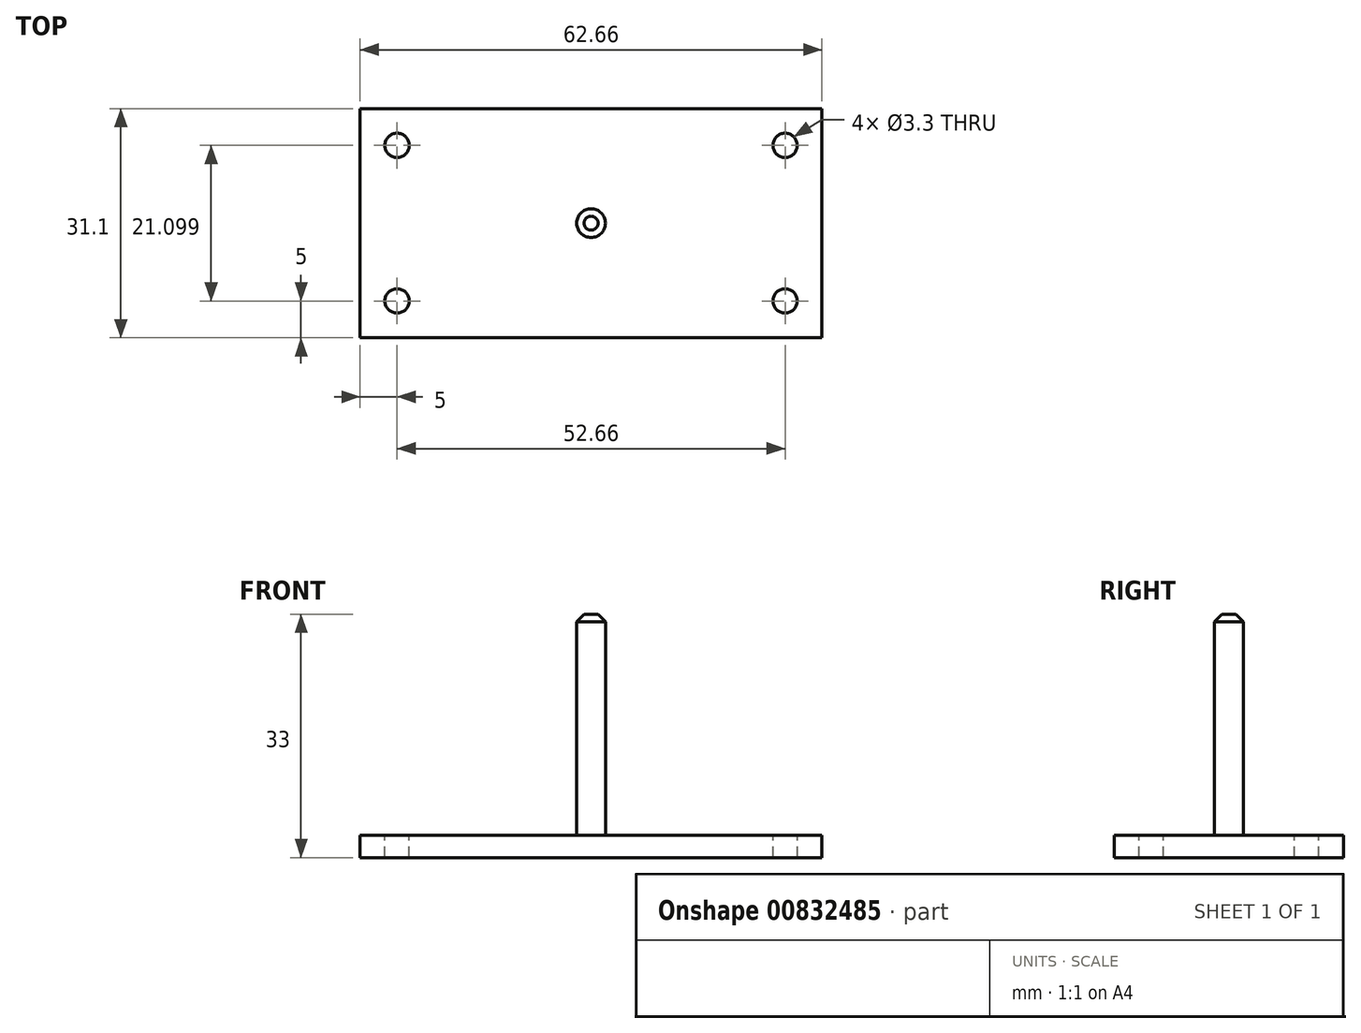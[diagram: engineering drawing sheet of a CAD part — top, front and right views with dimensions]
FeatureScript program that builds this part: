
annotation { "Feature Type Name" : "Feature", "Feature Type Description" : "" }
export const myFeature = defineFeature(function(context is Context, id is Id, definition is map)
    precondition{}
    {
        {
            var Q0;
            Q0=qCreatedBy(makeId("Top.planeOp"),FACE);
            var sketch = newSketch(context, id + "F0", { "sketchPlane" : qUnion([Q0])});
            skCircle(sketch, "E0", {"center": v(0, 0) * mm, "radius": 15 * mm});
            skCircle(sketch, "E1", {"center": v(0, 0) * mm, "radius": 1.95 * mm});
            skLineSegment(sketch, "E2.bottom", {"start": v(31.33, -15.55) * mm, "end": v(-31.33, -15.55) * mm});
            skLineSegment(sketch, "E2.top", {"start": v(31.33, 15.55) * mm, "end": v(-31.33, 15.55) * mm});
            skLineSegment(sketch, "E2.left", {"start": v(31.33, -15.55) * mm, "end": v(31.33, 15.55) * mm});
            skLineSegment(sketch, "E2.right", {"start": v(-31.33, -15.55) * mm, "end": v(-31.33, 15.55) * mm});
            skPoint(sketch, "E3", {"position": v(26.33, 10.55) * mm});
            skLineSegment(sketch, "E4", {"start": v(0, 13.06) * mm, "end": v(0, -9.28) * mm, "construction": true});
            skLineSegment(sketch, "E5", {"start": v(-7.34, 0) * mm, "end": v(7.3, 0) * mm, "construction": true});
            skPoint(sketch, "E6.MirrorP", {"position": v(-26.33, 10.55) * mm});
            skPoint(sketch, "E7.MirrorP", {"position": v(26.33, -10.55) * mm});
            skPoint(sketch, "E8.MirrorP", {"position": v(-26.33, -10.55) * mm});
            skSolve(sketch);
        }
        {
            var Q0;
            Q0=makeQuery(id+"F0.imprint","IMPRINT",FACE,{"disambiguationData":[TD([[makeQuery(id+"F0.imprint","IMPRINT",EDGE,{"derivedFrom":sQuery(id+"F0.wireOp",EDGE,"E1")}),1.0]])]});
            var Q1;
            Q1=sQuery(id+"F0.wireOp",EDGE,"E1");
            extrude(context, id + "F1", {"entities" : qUnion([Q0]), "surfaceEntities" : qUnion([Q1]), "depth" : 30 * mm, "offsetDistance" : 25 * mm});
        }
        {
            var Q0;
            Q0=makeQuery(id+"F1.opExtrude","CAP_EDGE",EDGE,{"disambiguationData":[OSD([sQuery(id+"F0.wireOp",EDGE,"E1")])],"isStart":false});
            chamfer(context, id + "F2", {"entities" : qUnion([Q0]), "width" : 1 * mm, "tangentPropagation" : true});
        }
        {
            var Q0;
            Q0=makeQuery(id+"F0.imprint","IMPRINT",FACE,{"disambiguationData":[TD([[makeQuery(id+"F0.imprint","IMPRINT",EDGE,{"derivedFrom":sQuery(id+"F0.wireOp",EDGE,"E0")}),-1.0]])]});
            var Q1;
            Q1=makeQuery(id+"F0.imprint","IMPRINT",FACE,{"disambiguationData":[TD([[makeQuery(id+"F0.imprint","IMPRINT",EDGE,{"derivedFrom":sQuery(id+"F0.wireOp",EDGE,"E0")}),1.0]])]});
            var Q2;
            Q2=makeQuery(id+"F0.imprint","IMPRINT",FACE,{"disambiguationData":[TD([[makeQuery(id+"F0.imprint","IMPRINT",EDGE,{"derivedFrom":sQuery(id+"F0.wireOp",EDGE,"E1")}),1.0]])]});
            extrude(context, id + "F3", {"entities" : qUnion([Q0, Q1, Q2]), "operationType" : NewBodyOperationType.ADD, "oppositeDirection" : true, "depth" : 3 * mm, "offsetDistance" : 25 * mm});
        }
        {
            var Q0;
            Q0=sQuery(id+"F0.wireOp",VERTEX,"E6.MirrorP");
            var Q1;
            Q1=sQuery(id+"F0.wireOp",VERTEX,"E3");
            var Q2;
            Q2=sQuery(id+"F0.wireOp",VERTEX,"E7.MirrorP");
            var Q3;
            Q3=sQuery(id+"F0.wireOp",VERTEX,"E8.MirrorP");
            var Q4;
            Q4=makeQuery(id+"F1.opExtrude","SWEPT_BODY",BODY,{"disambiguationData":[OSD([sQuery(id+"F0.wireOp",EDGE,"E1")])]});
            hole(context, id + "F4", {"style" : HoleStyle.SIMPLE, "endStyle" : HoleEndStyle.BLIND, "standardTappedOrClearance" : lookupTablePath({ "fit" : "Normal", "standard" : "ISO", "size" : "M3", "type" : "Clearance" }), "standardBlindInLast" : lookupTablePath({ "fit" : "Standard", "standard" : "ISO", "size" : "M3", "type" : "Clearance" }), "holeDiameter" : 3.3 * mm, "majorDiameter" : 5 * mm, "holeDepth" : 10 * mm, "isTappedThrough" : true, "tappedDepth" : 12 * mm, "tapClearance" : 3, "locations" : qUnion([Q0, Q1, Q2, Q3]), "scope" : qUnion([Q4])});
        }
    });
